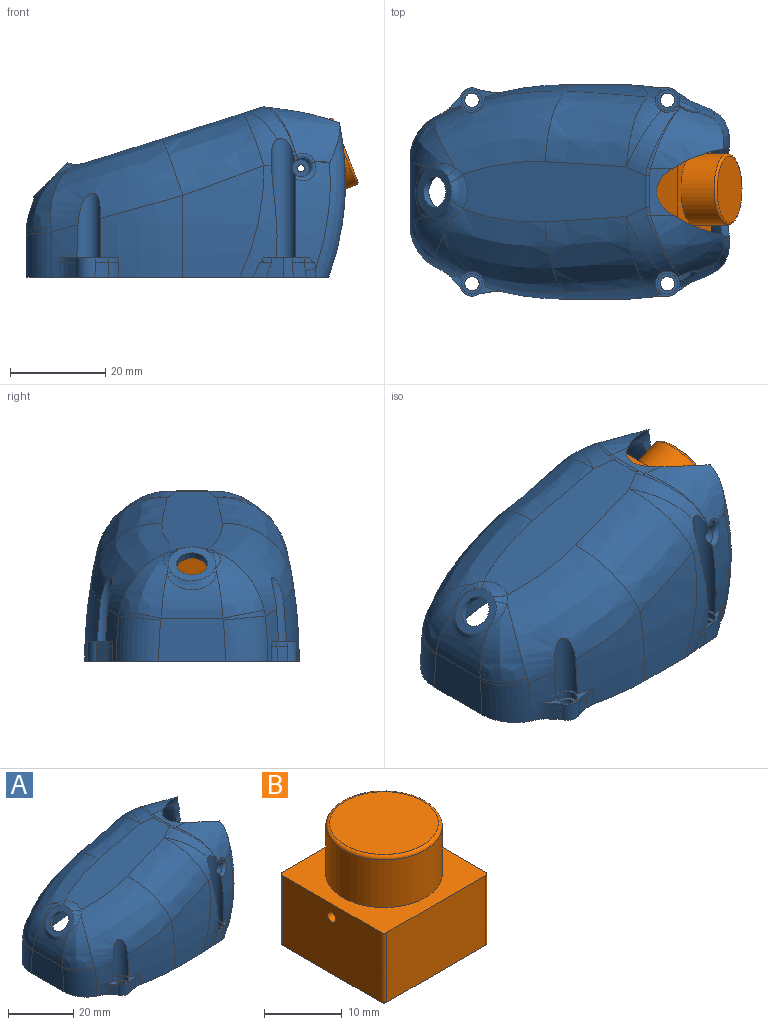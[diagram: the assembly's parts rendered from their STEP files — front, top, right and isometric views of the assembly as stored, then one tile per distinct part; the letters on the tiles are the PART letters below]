
ASSEMBLY  parts=2 mates=1
PART A: 226 faces, bbox 72.9x48x49.5 mm
  f0: cylinder r=1.5mm len=3mm, axis (0,0,-1), area 23.6mm2, adj f1,f225
  f1: plane 4.3x4.3mm, normal (0,0,1), area 7.5mm2, adj f0,f2
  f2: cylinder r=2.15mm len=4.3mm, axis (0,0,1), area 20.3mm2, adj f1,f3
  f3: plane 12.36x5.26mm, normal (0,0,1), area 11.5mm2, adj f2,f4,f216,f217,f218,f219,f220,f221
  f4: extruded ~3.83x1.02mm, area 4mm2, adj f3,f5,f216,f224
  f5: torus R=44mm, axis (-1,0,0), area 247.6mm2, adj f4,f6,f213,f214,f223,f224,f225
  f6: bspline ~39.11x22.46mm, area 489.8mm2, adj f5,f7,f208,f209,f210,f211,f212,f223
  f7: torus R=44mm, axis (-1,0,0), area 47.4mm2, adj f6,f8,f206,f221,f222,f223,f225
  f8: torus R=88.47mm, axis (1,0,0), area 99.4mm2, adj f7,f9,f208,f225
  f9: plane 13.93x9mm, normal (-1,0,0), area 122.6mm2, adj f8,f10,f204,f205,f208,f225
  f10: torus R=88.47mm, axis (1,0,0), area 99.4mm2, adj f9,f11,f204,f225
  f11: torus R=44mm, axis (-1,0,0), area 47.4mm2, adj f10,f12,f200,f201,f202,f203,f225
  f12: cylinder r=2.6mm len=1mm, axis (0,0,-1), area 0mm2, adj f11,f13,f203
  f13: plane 12.36x5.26mm, normal (0,0,1), area 11.5mm2, adj f12,f14,f15,f17,f193,f194,f195,f196
  f14: extruded ~1.61x1.23mm, area 2mm2, adj f13,f15,f202,f203
  f15: plane 2.18x1.9mm, normal (-0.75,0.66,0), area 2.9mm2, adj f13,f14,f16,f17
  f16: bspline ~3.45x3mm, area 8.6mm2, adj f15,f17,f202,f225
  f17: cylinder r=2.6mm len=4mm, axis (0,0,-1), area 19.5mm2, adj f13,f15,f16,f18,f193,f225
  f18: bspline ~3.91x3.45mm, area 8.6mm2, adj f17,f19,f193,f225
  f19: bspline ~4.26x2.09mm, area 6.1mm2, adj f18,f20,f194,f225
  f20: torus R=44mm, axis (-1,0,0), area 247.6mm2, adj f19,f21,f195,f196,f200,f201,f225
  f21: cylinder r=104mm len=23.36mm, axis (1,0,0), area 287.4mm2, adj f20,f22,f192,f225
  f22: bspline ~29x11.18mm, area 85.8mm2, adj f21,f23,f185,f186,f187,f188,f225
  f23: cylinder r=2.6mm len=25.01mm, axis (0,0,-1), area 228.7mm2, adj f22,f24,f181,f182,f183,f184,f185,f188
  f24: bspline ~27.14x17.69mm, area 130.4mm2, adj f23,f25,f178,f179,f180,f184,f188
  f25: bspline ~39.15x9.1mm, area 174.2mm2, adj f24,f26,f172,f173,f178,f225
  f26: cylinder r=59.23mm len=32.36mm, axis (0,-1,0), area 410.2mm2, adj f25,f27,f165,f166,f167,f168,f169,f170
  f27: cylinder r=9.5mm len=19mm, axis (0.97,0,0.26), area 54.1mm2, adj f26,f28,f165,f171
  f28: cylinder r=57.73mm len=26.72mm, axis (0,-1,0), area 383.9mm2, adj f27,f29,f160,f161,f164,f165,f171,f225
  f29: bspline ~16.44x9.11mm, area 48.7mm2, adj f28,f30,f31,f159,f165,f166,f169
  f30: bspline ~5.72x2.43mm, area 0.1mm2, adj f29,f159,f160
  f31: offset ~20x17.92mm, area 98mm2, adj f29,f32,f153,f157,f158,f169
  f32: bspline ~12.37x7.64mm, area 1mm2, adj f31,f33,f34,f153
  f33: bspline ~3.03x0.76mm, area 0.1mm2, adj f32,f34,f158,f169
  f34: bspline ~16.38x15.8mm, area 52.7mm2, adj f32,f33,f35,f150,f151,f152,f153,f169
  f35: plane 7.69x0.79mm, normal (0.97,0,0.26), area 4.2mm2, adj f34,f36,f150,f169
  f36: bspline ~16.43x15.82mm, area 52.7mm2, adj f35,f37,f109,f147,f148,f149,f150,f169
  f37: bspline ~12.36x7.6mm, area 1mm2, adj f36,f38,f109,f149
  f38: offset ~20x17.92mm, area 97.9mm2, adj f37,f39,f108,f109,f164,f169
  f39: bspline ~5.65x2.19mm, area 0mm2, adj f38,f40,f106,f109
  f40: offset ~35.1x22.52mm, area 71.3mm2, adj f39,f41,f106,f109,f161,f225
  f41: bspline ~21.84x3.5mm, area 58.2mm2, adj f40,f42,f109,f225
  f42: cylinder r=2.75mm len=26.09mm, axis (0,0,-1), area 112.7mm2, adj f41,f43,f44,f104,f105,f109,f147,f225
  f43: bspline ~4.82x3.66mm, area 9.7mm2, adj f42,f44,f147,f148
  f44: bspline ~4x2.78mm, area 4.2mm2, adj f42,f43,f45,f104
  f45: bspline ~21.1x16.03mm, area 336.7mm2, adj f44,f46,f103,f148,f150
  f46: cylinder r=102.5mm len=22.79mm, axis (1,0,0), area 295mm2, adj f45,f47,f48,f104,f225
  f47: bspline ~16.27x9.62mm, area 20.5mm2, adj f46,f105,f225
  f48: torus R=44mm, axis (-1,0,0), area 229.4mm2, adj f46,f49,f103,f225
  f49: bspline ~18.03x2.34mm, area 31.3mm2, adj f48,f50,f102,f225
  f50: cylinder r=2.7mm len=15.52mm, axis (0,0,-1), area 57.3mm2, adj f49,f51,f102,f225
  f51: bspline ~13.69x3.04mm, area 26.7mm2, adj f50,f52,f102,f225
  f52: torus R=44mm, axis (-1,0,0), area 39.3mm2, adj f51,f53,f103,f225
  f53: torus R=88.47mm, axis (1,0,0), area 83.8mm2, adj f52,f54,f101,f225
  f54: plane 13.93x9mm, normal (1,0,0), area 122.6mm2, adj f53,f55,f99,f100,f101,f225
  f55: cylinder r=13.5mm len=12.98mm, axis (0,-1,0), area 80.4mm2, adj f54,f56,f95,f96,f97,f98
  f56: bspline ~15.43x10.96mm, area 84.4mm2, adj f55,f57,f73,f77,f78,f99
  f57: cylinder r=13.5mm len=7.04mm, axis (0,-1,0), area 5mm2, adj f56,f58,f72,f73,f98,f150
  f58: plane 4.1x2.61mm, normal (-0.61,0.5,-0.61), area 5.7mm2, adj f57,f59,f71,f72,f73
  f59: plane 8.2x6.7mm, normal (0.71,0,-0.71), area 25mm2, adj f58,f60,f61,f62,f63,f71,f72
  f60: plane 4.2x4.2mm, normal (0,-1,0), area 5.7mm2, adj f59,f61,f72,f73
  f61: plane 4.1x2.52mm, normal (0.61,-0.5,0.61), area 5.7mm2, adj f59,f60,f62,f73
  f62: plane 4.1x2.52mm, normal (0.61,0.5,0.61), area 5.7mm2, adj f59,f61,f71,f73
  f63: cylinder r=3.25mm len=6.5mm, axis (-0.71,0,0.71), area 30.6mm2, adj f59,f64
  f64: plane 10.27x7.35mm, normal (-0.71,0,0.71), area 45.4mm2, adj f63,f65,f66,f67,f69,f70,f210
  f65: bspline ~6.69x5.16mm, area 8.6mm2, adj f64,f66,f209,f210
  f66: bspline ~10.31x3.68mm, area 20.4mm2, adj f64,f65,f67,f205
  f67: bspline ~6.41x4.99mm, area 8.6mm2, adj f64,f66,f68,f69
  f68: bspline ~17.14x12.31mm, area 109mm2, adj f67,f201,f204,f205
  f69: bspline ~3.12x3.05mm, area 4.9mm2, adj f64,f67,f70,f201
  f70: bspline ~7.08x3.61mm, area 18.6mm2, adj f64,f69,f210,f211
  f71: plane 4.2x4.2mm, normal (0,1,0), area 5.7mm2, adj f58,f59,f62,f73
  f72: plane 4.1x2.61mm, normal (-0.61,-0.5,-0.61), area 5.7mm2, adj f57,f58,f59,f60,f73
  f73: plane 10.14x6.83mm, normal (0.71,0,-0.71), area 20.9mm2, adj f56,f57,f58,f60,f61,f62,f71,f72
  f74: cylinder r=5mm len=3.79mm, axis (-0.71,0,0.71), area 0.9mm2, adj f73,f77,f95
  f75: cylinder r=5mm len=3.79mm, axis (-0.71,0,0.71), area 0.9mm2, adj f73,f76,f97
  f76: bspline ~6.66x5.3mm, area 8.8mm2, adj f73,f75,f97,f98
  f77: bspline ~6.18x4.73mm, area 8.8mm2, adj f56,f73,f74,f95
  f78: bspline ~37.96x21.08mm, area 426.5mm2, adj f56,f79,f83,f84,f94,f99,f150
  f79: torus R=44mm, axis (-1,0,0), area 39.3mm2, adj f78,f80,f100,f225
  f80: bspline ~13.69x3.04mm, area 26.7mm2, adj f79,f81,f83,f225
  f81: cylinder r=2.7mm len=15.52mm, axis (0,0,-1), area 57.3mm2, adj f80,f82,f83,f225
  f82: bspline ~18.03x2.34mm, area 31.3mm2, adj f81,f83,f84,f225
  f83: bspline ~7.82x7.37mm, area 24.2mm2, adj f78,f80,f81,f82
  f84: torus R=44mm, axis (-1,0,0), area 229.4mm2, adj f78,f82,f85,f225
  f85: cylinder r=102.5mm len=22.79mm, axis (1,0,0), area 295mm2, adj f84,f86,f93,f94,f225
  f86: bspline ~17.08x10.05mm, area 20.5mm2, adj f85,f87,f225
  f87: bspline ~11.84x2.97mm, area 35.2mm2, adj f86,f88,f93,f225
  f88: cylinder r=2.75mm len=26.09mm, axis (0,0,-1), area 112.7mm2, adj f87,f89,f90,f91,f93,f152,f153,f225
  f89: bspline ~6.24x2.93mm, area 4.2mm2, adj f88,f90,f93,f94
  f90: bspline ~5.61x3.87mm, area 9.7mm2, adj f88,f89,f151,f152
  f91: bspline ~21.84x3.5mm, area 58.2mm2, adj f88,f92,f153,f225
  f92: offset ~35.1x22.52mm, area 71.3mm2, adj f91,f153,f157,f159,f160,f225
  f93: bspline ~19.15x3.75mm, area 46.4mm2, adj f85,f87,f88,f89
  f94: bspline ~21.1x16.03mm, area 336.7mm2, adj f78,f85,f89,f150,f151
  f95: bspline ~3.23x3.14mm, area 2.7mm2, adj f55,f74,f77,f96
  f96: bspline ~7.9x1.83mm, area 9.5mm2, adj f55,f73,f95,f97
  f97: bspline ~2.93x2.76mm, area 2.7mm2, adj f55,f75,f76,f96
  f98: bspline ~15.43x10.96mm, area 84.3mm2, adj f55,f57,f73,f76,f101,f103
  f99: bspline ~7.82x4.81mm, area 7.6mm2, adj f54,f56,f78,f100
  f100: torus R=88.47mm, axis (1,0,0), area 83.8mm2, adj f54,f79,f99,f225
  f101: bspline ~7.79x4.68mm, area 7.6mm2, adj f53,f54,f98,f103
  f102: bspline ~7.83x7.37mm, area 24.2mm2, adj f49,f50,f51,f103
  f103: bspline ~37.96x21.08mm, area 426.5mm2, adj f45,f48,f52,f98,f101,f102,f150
  f104: bspline ~16.27x3.56mm, area 46.4mm2, adj f42,f44,f46,f105
  f105: bspline ~11.84x2.97mm, area 35.2mm2, adj f42,f47,f104,f225
  f106: bspline ~0.77x0.37mm, area 0mm2, adj f39,f40,f107,f164
  f107: bspline ~1.29x0.55mm, area 0mm2, adj f106,f161,f164
  f108: plane 1.44x1.09mm, normal (-0.13,0,-0.99), area 0.6mm2, adj f38,f149,f169
  f109: cone r=2.5mm half-angle=21deg, axis (0,-1,0), area 138mm2, adj f36,f37,f38,f39,f40,f41,f42,f110
  f110: plane 5x5mm, normal (0,1,0), area 17.9mm2, adj f109,f111
  f111: cylinder r=0.75mm len=1.5mm, axis (0,1,0), area 4.7mm2, adj f110,f112
  f112: plane 3.6x3.6mm, normal (0,-1,0), area 8.4mm2, adj f111,f113
  f113: cylinder r=1.8mm len=7.13mm, axis (0,1,0), area 65.2mm2, adj f112,f114,f142,f143,f144,f145,f146
  f114: cylinder r=2.6mm len=25.01mm, axis (0,0,-1), area 228.7mm2, adj f113,f115,f125,f129,f131,f141,f142,f146
  f115: bspline ~28.19x10.76mm, area 85.8mm2, adj f114,f116,f124,f125,f141,f213,f225
  f116: extruded ~2.42x1mm, area 2mm2, adj f115,f117,f124,f125
  f117: plane 4x3.69mm, normal (0.05,-1,0), area 11.9mm2, adj f116,f118,f124,f125,f225
  f118: cylinder r=2.6mm len=4mm, axis (0,0,-1), area 8.9mm2, adj f117,f119,f123,f125,f225
  f119: plane 2.46x1.71mm, normal (0.57,-0.82,0), area 3mm2, adj f118,f120,f123,f125
  f120: extruded ~2.15x1.14mm, area 1.9mm2, adj f119,f121,f125,f129
  f121: bspline ~2.81x2.47mm, area 3.7mm2, adj f120,f122,f123,f129
  f122: bspline ~4.09x2.36mm, area 3.6mm2, adj f121,f123,f167,f225
  f123: bspline ~4.07x2.84mm, area 9.5mm2, adj f118,f119,f121,f122,f225
  f124: bspline ~5.98x4.26mm, area 7.9mm2, adj f115,f116,f117,f225
  f125: plane 9.68x5.49mm, normal (0,0,1), area 8.8mm2, adj f114,f115,f116,f117,f118,f119,f120,f126
  f126: cylinder r=2.15mm len=4.3mm, axis (0,0,1), area 20.3mm2, adj f125,f127
  f127: plane 4.3x4.3mm, normal (0,0,1), area 7.5mm2, adj f126,f128
  f128: cylinder r=1.5mm len=3mm, axis (0,0,-1), area 23.6mm2, adj f127,f225
  f129: bspline ~27.14x17.69mm, area 130.4mm2, adj f114,f120,f121,f125,f130,f142,f167
  f130: bspline ~5.65x2.18mm, area 0.1mm2, adj f129,f143,f167,f168
  f131: bspline ~17.41x17.18mm, area 59mm2, adj f114,f132,f140,f141,f146,f211
  f132: bspline ~4.35x1.42mm, area 1.3mm2, adj f131,f133,f139,f140
  f133: plane 9.79x4.93mm, normal (0.13,0,0.99), area 25.1mm2, adj f132,f134,f139,f168,f169,f172
  f134: bspline ~4.35x1.42mm, area 1.3mm2, adj f133,f135,f139,f181
  f135: bspline ~12.96x10.27mm, area 6.6mm2, adj f134,f136,f172,f181
  f136: bspline ~1.25x1.09mm, area 0.1mm2, adj f135,f137,f182,f183
  f137: bspline ~3.88x2.41mm, area 7.1mm2, adj f136,f138,f172,f183
  f138: bspline ~1.57x1.35mm, area 0.1mm2, adj f137,f178,f183,f184
  f139: cylinder r=1.8mm len=6.64mm, axis (0,1,0), area 5.3mm2, adj f132,f133,f134,f211
  f140: bspline ~12.95x10.22mm, area 6.6mm2, adj f131,f132,f145,f168
  f141: sphere r=15mm, area 49.9mm2, adj f114,f115,f131,f212
  f142: bspline ~5.13x4.27mm, area 10.1mm2, adj f113,f114,f129,f143
  f143: bspline ~1.57x1.36mm, area 0.1mm2, adj f113,f130,f142,f144
  f144: bspline ~4.51x2.51mm, area 7.1mm2, adj f113,f143,f145,f168
  f145: bspline ~1.27x1.11mm, area 0.1mm2, adj f113,f140,f144,f146
  f146: bspline ~2.44x2.26mm, area 1.6mm2, adj f113,f114,f131,f145
  f147: bspline ~3.59x2.6mm, area 3.5mm2, adj f36,f42,f43,f109
  f148: sphere r=13.5mm, area 61.4mm2, adj f36,f43,f45
  f149: bspline ~3.03x0.76mm, area 0.1mm2, adj f36,f37,f108,f169
  f150: plane 38.8x12.71mm, normal (0.3,0,-0.95), area 447.1mm2, adj f34,f35,f36,f45,f57,f78,f94,f103
  f151: sphere r=13.5mm, area 61.4mm2, adj f34,f90,f94
  f152: bspline ~4.15x2.72mm, area 3.5mm2, adj f34,f88,f90,f153
  f153: cone r=2.5mm half-angle=21deg, axis (0,1,0), area 138mm2, adj f31,f32,f34,f88,f91,f92,f152,f154
  f154: plane 5x5mm, normal (0,-1,0), area 17.9mm2, adj f153,f155
  f155: cylinder r=0.75mm len=1.5mm, axis (0,-1,0), area 4.7mm2, adj f154,f156
  f156: plane 3.6x3.6mm, normal (0,1,0), area 8.4mm2, adj f155,f183
  f157: bspline ~5.65x2.19mm, area 0mm2, adj f31,f92,f153,f159
  f158: plane 1.44x1.09mm, normal (-0.13,0,-0.99), area 0.6mm2, adj f31,f33,f169
  f159: bspline ~0.77x0.37mm, area 0mm2, adj f29,f30,f92,f157
  f160: bspline ~26.22x6.61mm, area 89mm2, adj f28,f30,f92,f225
  f161: bspline ~26.04x6.54mm, area 89mm2, adj f28,f40,f107,f162,f163,f225
  f162: bspline ~3.65x2.34mm, area 0mm2, adj f161,f164
  f163: bspline ~0.4x0.21mm, area 0mm2, adj f161,f164
  f164: bspline ~16.44x9.11mm, area 48.8mm2, adj f28,f38,f106,f107,f162,f163,f169,f170
  f165: cylinder r=9.5mm len=4.18mm, axis (0.97,0,0.26), area 5.7mm2, adj f26,f27,f28,f29,f166
  f166: cylinder r=2mm len=1.75mm, axis (0.97,0,0.26), area 1.1mm2, adj f26,f29,f165,f169
  f167: bspline ~38.79x9.08mm, area 174.2mm2, adj f26,f122,f129,f130,f168,f225
  f168: bspline ~17x14.71mm, area 166.1mm2, adj f26,f130,f133,f140,f144,f167,f169
  f169: cylinder r=9.5mm len=19mm, axis (0.97,0,0.26), area 105.5mm2, adj f26,f29,f31,f33,f34,f35,f36,f38
  f170: cylinder r=2mm len=1.75mm, axis (0.97,0,0.26), area 1.1mm2, adj f26,f164,f169,f171
  f171: cylinder r=9.5mm len=4.18mm, axis (0.97,0,0.26), area 5.7mm2, adj f26,f27,f28,f164,f170
  f172: bspline ~17x14.71mm, area 166.1mm2, adj f25,f26,f133,f135,f137,f169,f178
  f173: bspline ~4.1x2.36mm, area 3.6mm2, adj f25,f174,f180,f225
  f174: bspline ~4.07x2.84mm, area 9.5mm2, adj f173,f175,f177,f180,f225
  f175: cylinder r=2.6mm len=4mm, axis (0,0,-1), area 8.9mm2, adj f174,f176,f177,f188,f225
  f176: plane 4x3.69mm, normal (0.05,1,0), area 11.9mm2, adj f175,f186,f187,f188,f225
  f177: plane 2.46x1.71mm, normal (0.57,0.82,0), area 3mm2, adj f174,f175,f179,f188
  f178: bspline ~5.65x2.18mm, area 0.1mm2, adj f24,f25,f138,f172
  f179: extruded ~2.15x1.14mm, area 1.9mm2, adj f24,f177,f180,f188
  f180: bspline ~2.82x2.47mm, area 3.7mm2, adj f24,f173,f174,f179
  f181: bspline ~19.38x18.1mm, area 58.7mm2, adj f23,f134,f135,f182,f185,f211
  f182: bspline ~2.44x2.26mm, area 1.6mm2, adj f23,f136,f181,f183
  f183: cylinder r=1.8mm len=7.13mm, axis (0,-1,0), area 65.2mm2, adj f23,f136,f137,f138,f156,f182,f184
  f184: bspline ~5.13x4.06mm, area 10.1mm2, adj f23,f24,f138,f183
  f185: sphere r=15mm, area 49.9mm2, adj f22,f23,f181,f192
  f186: bspline ~6.19x4.38mm, area 7.9mm2, adj f22,f176,f187,f225
  f187: extruded ~2.42x1mm, area 2mm2, adj f22,f176,f186,f188
  f188: plane 9.68x5.49mm, normal (0,0,1), area 8.8mm2, adj f22,f23,f24,f175,f176,f177,f179,f187
  f189: cylinder r=2.15mm len=4.3mm, axis (0,0,1), area 20.3mm2, adj f188,f190
  f190: plane 4.3x4.3mm, normal (0,0,1), area 7.5mm2, adj f189,f191
  f191: cylinder r=1.5mm len=3mm, axis (0,0,-1), area 23.6mm2, adj f190,f225
  f192: bspline ~21.55x17.21mm, area 375.1mm2, adj f21,f185,f201,f211
  f193: plane 2.85x1mm, normal (0.18,0.98,0), area 2.9mm2, adj f13,f17,f18,f194
  f194: extruded ~2.03x1mm, area 2mm2, adj f13,f19,f193,f195
  f195: extruded ~3.83x1.02mm, area 4mm2, adj f13,f20,f194,f196
  f196: cylinder r=2.6mm len=1mm, axis (0,0,-1), area 0mm2, adj f13,f20,f195
  f197: cylinder r=2.15mm len=4.3mm, axis (0,0,1), area 20.3mm2, adj f13,f198
  f198: plane 4.3x4.3mm, normal (0,0,1), area 7.5mm2, adj f197,f199
  f199: cylinder r=1.5mm len=3mm, axis (0,0,-1), area 23.6mm2, adj f198,f225
  f200: cylinder r=2.6mm len=13.53mm, axis (0,0,-1), area 82.1mm2, adj f11,f13,f20,f201
  f201: bspline ~39.11x22.46mm, area 489.8mm2, adj f11,f20,f68,f69,f192,f200,f204,f211
  f202: bspline ~4.28x1.63mm, area 6.1mm2, adj f11,f14,f16,f225
  f203: extruded ~3.64x1.59mm, area 4mm2, adj f11,f12,f13,f14
  f204: bspline ~9.17x5.66mm, area 9.6mm2, adj f9,f10,f68,f201
  f205: cylinder r=15mm len=12.98mm, axis (0,-1,0), area 86.2mm2, adj f9,f66,f68,f209
  f206: bspline ~4.26x1.64mm, area 6.1mm2, adj f7,f207,f220,f225
  f207: bspline ~3.45x3mm, area 8.6mm2, adj f206,f218,f219,f225
  f208: bspline ~9.13x5.5mm, area 9.6mm2, adj f6,f8,f9,f209
  f209: bspline ~17.14x12.31mm, area 109mm2, adj f6,f65,f205,f208
  f210: bspline ~3.12x3.05mm, area 4.9mm2, adj f6,f64,f65,f70
  f211: plane 38.43x12.71mm, normal (-0.3,0,0.95), area 439.3mm2, adj f6,f70,f131,f139,f181,f192,f201,f212
  f212: bspline ~21.55x17.21mm, area 375.1mm2, adj f6,f141,f211,f213
  f213: cylinder r=104mm len=23.36mm, axis (1,0,0), area 287.4mm2, adj f5,f115,f212,f225
  f214: bspline ~4.28x2.08mm, area 6.1mm2, adj f5,f215,f216,f225
  f215: bspline ~3.91x3.45mm, area 8.6mm2, adj f214,f217,f218,f225
  f216: extruded ~2.03x1mm, area 2mm2, adj f3,f4,f214,f217
  f217: plane 2.85x1mm, normal (0.18,-0.98,0), area 2.9mm2, adj f3,f215,f216,f218
  f218: cylinder r=2.6mm len=4mm, axis (0,0,-1), area 19.5mm2, adj f3,f207,f215,f217,f219,f225
  f219: plane 2.18x1.9mm, normal (-0.75,-0.66,0), area 2.9mm2, adj f3,f207,f218,f220
  f220: extruded ~1.61x1.23mm, area 2mm2, adj f3,f206,f219,f221
  f221: extruded ~3.64x1.59mm, area 4mm2, adj f3,f7,f220,f222
  f222: cylinder r=2.6mm len=1mm, axis (0,0,-1), area 0mm2, adj f3,f7,f221
  f223: cylinder r=2.6mm len=13.53mm, axis (0,0,-1), area 82.1mm2, adj f3,f5,f6,f7
  f224: cylinder r=2.6mm len=1mm, axis (0,0,-1), area 0mm2, adj f3,f4,f5
  f225: plane 63.86x45.36mm, normal (0,0,-1), area 342.5mm2, adj f0,f5,f7,f8,f9,f10,f11,f16
PART B: 14 faces, bbox 19x19x19 mm
  f0: plane 18x11mm, normal (0,1,0), area 198mm2, adj f4,f5,f10,f13
  f1: plane 18x11mm, normal (-1,0,0), area 196.2mm2, adj f4,f5,f9,f10,f11
  f2: plane 18x11mm, normal (0,-1,0), area 198mm2, adj f4,f5,f11,f12
  f3: plane 18x11mm, normal (1,0,0), area 196.2mm2, adj f4,f5,f9,f12,f13
  f4: plane 19x19mm, normal (0,0,1), area 184.1mm2, adj f0,f1,f2,f3,f6,f10,f11,f12
  f5: plane 19x19mm, normal (0,0,-1), area 360.8mm2, adj f0,f1,f2,f3,f10,f11,f12,f13
  f6: cylinder r=7.5mm len=15mm, axis (0,0,-1), area 353.4mm2, adj f4,f8
  f7: plane 14x14mm, normal (0,0,1), area 153.9mm2, adj f8
  f8: torus R=7mm, axis (0,0,1), area 36.1mm2, adj f6,f7
  f9: cylinder r=0.75mm len=19mm, axis (1,0,0), area 89.5mm2, adj f1,f3
  f10: cylinder r=0.5mm len=11mm, axis (0,0,1), area 8.6mm2, adj f0,f1,f4,f5
  f11: cylinder r=0.5mm len=11mm, axis (0,0,-1), area 8.6mm2, adj f1,f2,f4,f5
  f12: cylinder r=0.5mm len=11mm, axis (0,0,1), area 8.6mm2, adj f2,f3,f4,f5
  f13: cylinder r=0.5mm len=11mm, axis (0,0,-1), area 8.6mm2, adj f0,f3,f4,f5
PLACE A t=(-55.35,-17.28,8.93)mm fixed
PLACE B rot(axis=(-0.49,0.49,-0.72),108.4deg) t=(-49.25,-20.4,24.71)mm
MATE revolute A.f183 <-> B.f9  axis (0,-1,0) through (-42.42,-2.21,31.72)mm
